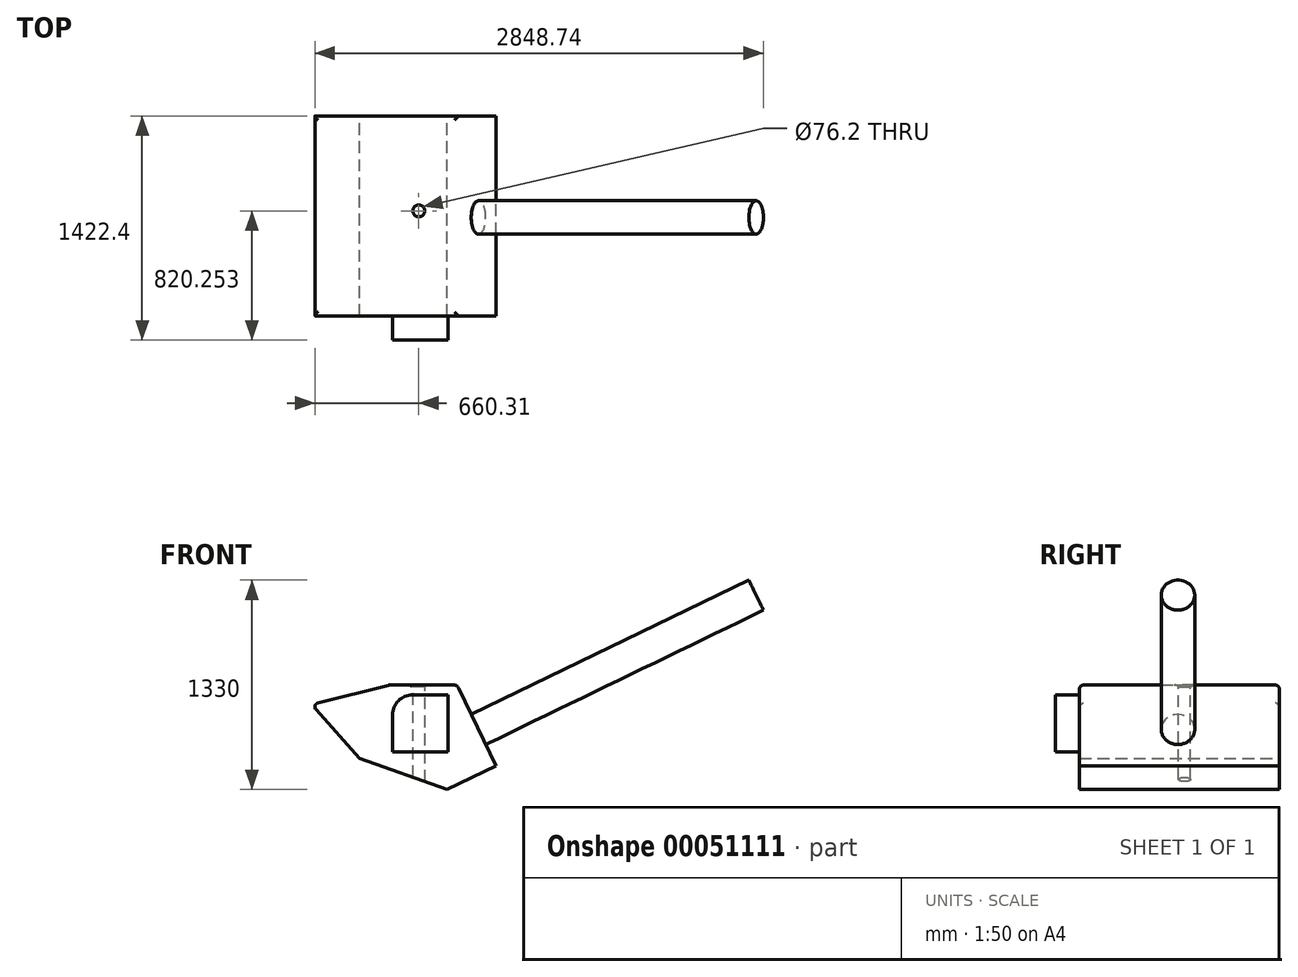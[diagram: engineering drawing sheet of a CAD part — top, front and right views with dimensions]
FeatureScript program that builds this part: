
annotation { "Feature Type Name" : "Feature", "Feature Type Description" : "" }
export const myFeature = defineFeature(function(context is Context, id is Id, definition is map)
    precondition{}
    {
        {
            var Q0;
            Q0=qCreatedBy(makeId("Front.planeOp"),FACE);
            var sketch = newSketch(context, id + "F0", { "sketchPlane" : qUnion([Q0])});
            skLineSegment(sketch, "E0", {"start": v(-562.47, 161.35) * mm, "end": v(-69.75, 285.02) * mm});
            skLineSegment(sketch, "E1", {"start": v(-69.75, 285.02) * mm, "end": v(362.05, 285.02) * mm});
            skLineSegment(sketch, "E2", {"start": v(362.05, 285.02) * mm, "end": v(609.8, -226.85) * mm});
            skLineSegment(sketch, "E3", {"start": v(609.8, -226.85) * mm, "end": v(297.88, -377.82) * mm});
            skLineSegment(sketch, "E4", {"start": v(297.88, -377.82) * mm, "end": v(-257.82, -179.56) * mm});
            skLineSegment(sketch, "E5", {"start": v(-257.82, -179.56) * mm, "end": v(-562.47, 161.35) * mm});
            skSolve(sketch);
        }
        {
            var Q0;
            Q0=makeQuery(id+"F0.imprint","IMPRINT",FACE,{"disambiguationData":[TD([[makeQuery(id+"F0.imprint","IMPRINT",EDGE,{"derivedFrom":sQuery(id+"F0.wireOp",EDGE,"E0")}),-1.0]])]});
            extrude(context, id + "F1", {"entities" : qUnion([Q0]), "depth" : 1270 * mm});
        }
        {
            var Q0;
            Q0=makeQuery(id+"F1.opExtrude","CAP_FACE",FACE,{"disambiguationData":[OSD([sQuery(id+"F0.wireOp",EDGE,"E0"),sQuery(id+"F0.wireOp",EDGE,"E1"),sQuery(id+"F0.wireOp",EDGE,"E2"),sQuery(id+"F0.wireOp",EDGE,"E3"),sQuery(id+"F0.wireOp",EDGE,"E4"),sQuery(id+"F0.wireOp",EDGE,"E5")])],"isStart":false});
            var sketch = newSketch(context, id + "F2", { "sketchPlane" : qUnion([Q0])});
            skLineSegment(sketch, "E6.bottom", {"start": v(79.33, 222.86) * mm, "end": v(304.25, 222.86) * mm});
            skLineSegment(sketch, "E6.top", {"start": v(-47.67, -137.95) * mm, "end": v(304.25, -137.95) * mm});
            skLineSegment(sketch, "E6.left", {"start": v(-47.67, 95.86) * mm, "end": v(-47.67, -137.95) * mm});
            skLineSegment(sketch, "E6.right", {"start": v(304.25, 222.86) * mm, "end": v(304.25, -137.95) * mm});
            skPoint(sketch, "E7.visualSharp", {"position": v(-47.67, 222.86) * mm});
            skArc(sketch, "E7.filletArc", {"start": v(79.33, 222.86) * mm, "mid": v(-10.47, 185.67) * mm, "end": v(-47.67, 95.86) * mm});
            skSolve(sketch);
        }
        {
            var Q0;
            Q0=makeQuery(id+"F2.imprint","IMPRINT",FACE,{"disambiguationData":[TD([[makeQuery(id+"F2.imprint","IMPRINT",EDGE,{"derivedFrom":sQuery(id+"F2.wireOp",EDGE,"E6.bottom")}),-1.0]])]});
            extrude(context, id + "F3", {"entities" : qUnion([Q0]), "operationType" : NewBodyOperationType.ADD, "depth" : 152.4 * mm});
        }
        {
            var Q0;
            Q0=makeQuery(id+"F1.opExtrude","SWEPT_FACE",FACE,{"disambiguationData":[OSD([sQuery(id+"F0.wireOp",EDGE,"E2")])]});
            var sketch = newSketch(context, id + "F4", { "sketchPlane" : qUnion([Q0])});
            skCircle(sketch, "E8", {"center": v(-644.19, -214.23) * mm, "radius": 106.18 * mm});
            skSolve(sketch);
        }
        {
            var Q0;
            Q0 = qSketchRegion(id + "F4", true);
            extrude(context, id + "F5", {"entities" : qUnion([Q0]), "operationType" : NewBodyOperationType.ADD, "endBound" : BoundingType.THROUGH_ALL, "depth" : 25.4 * mm});
        }
        {
            var Q0;
            Q0=makeQuery(id+"F1.opExtrude","SWEPT_FACE",FACE,{"disambiguationData":[OSD([sQuery(id+"F0.wireOp",EDGE,"E1")])]});
            var sketch = newSketch(context, id + "F6", { "sketchPlane" : qUnion([Q0])});
            skCircle(sketch, "E9", {"center": v(119.38, -602.15) * mm, "radius": 84.9 * mm});
            skSolve(sketch);
        }
        {
            var Q0;
            Q0=sQuery(id+"F6.wireOp",VERTEX,"E9.center");
            var Q1;
            Q1=makeQuery(id+"F1.opExtrude","SWEPT_BODY",BODY,{"disambiguationData":[OSD([sQuery(id+"F0.wireOp",EDGE,"E0"),sQuery(id+"F0.wireOp",EDGE,"E1"),sQuery(id+"F0.wireOp",EDGE,"E2"),sQuery(id+"F0.wireOp",EDGE,"E3"),sQuery(id+"F0.wireOp",EDGE,"E4"),sQuery(id+"F0.wireOp",EDGE,"E5")])]});
            hole(context, id + "F7", {"style" : HoleStyle.C_SINK, "holeDiameter" : 76.2 * mm, "cSinkDiameter" : 101.6 * mm, "endStyle" : HoleEndStyle.THROUGH, "locations" : qUnion([Q0]), "scope" : qUnion([Q1]), "cSinkAngle" : 90 * degree});
        }
        {
            var Q0;
            Q0=makeQuery(id+"F1.opExtrude","SWEPT_FACE",FACE,{"disambiguationData":[OSD([sQuery(id+"F0.wireOp",EDGE,"E0")])]});
            var Q1;
            Q1=makeQuery(id+"F1.opExtrude","SWEPT_FACE",FACE,{"disambiguationData":[OSD([sQuery(id+"F0.wireOp",EDGE,"E1")])]});
            fillet(context, id + "F8", {"entities" : qUnion([Q0, Q1]), "radius" : 25.4 * mm, "tangentPropagation" : true, "allowEdgeOverflow" : false});
        }
    });
